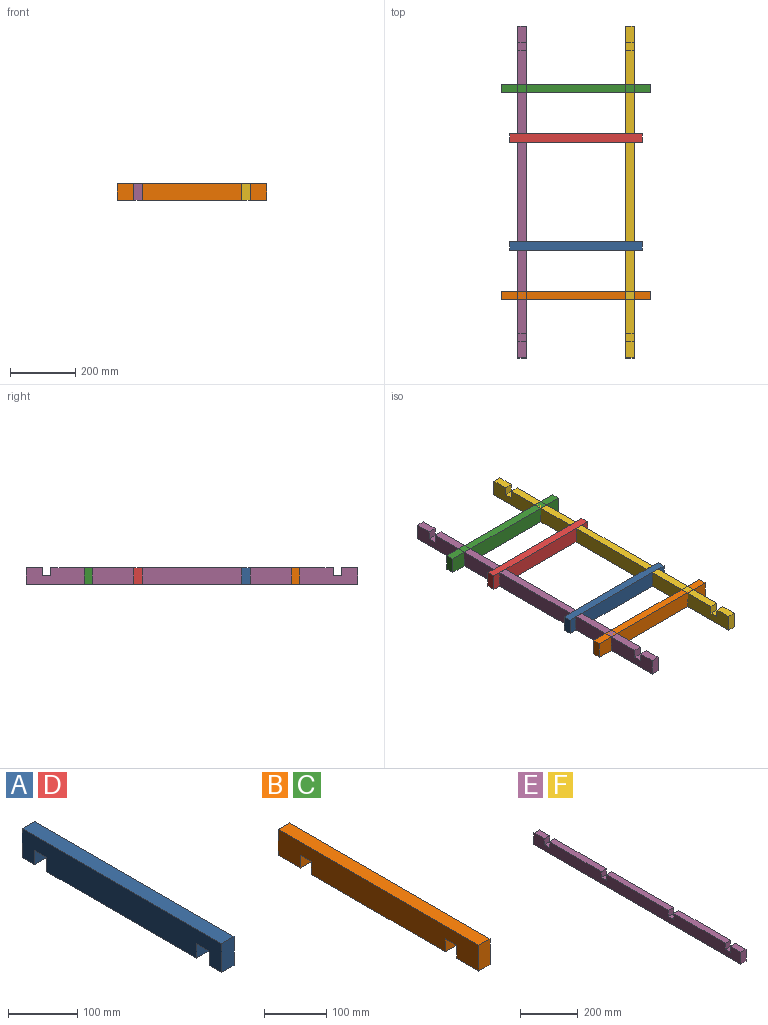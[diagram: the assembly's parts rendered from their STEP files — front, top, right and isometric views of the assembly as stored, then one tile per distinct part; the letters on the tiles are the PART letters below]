
ASSEMBLY  parts=6 mates=2
PART A: 14 faces, bbox 25.4x406.4x50.8 mm
  f0: plane 304.8x25.4mm, normal (0,0,-1), area 7741.9mm2, adj f2,f3,f9,f11
  f1: plane 25.4x25.4mm, normal (0,0,-1), area 645.2mm2, adj f2,f3,f6,f10
  f2: plane 406.4x50.8mm, normal (1,0,0), area 19354.8mm2, adj f0,f1,f4,f5,f6,f7,f8,f9
  f3: plane 406.4x50.8mm, normal (-1,0,0), area 19354.8mm2, adj f0,f1,f4,f5,f6,f7,f8,f9
  f4: plane 50.8x25.4mm, normal (0,-1,0), area 1290.3mm2, adj f2,f3,f5,f7
  f5: plane 25.4x25.4mm, normal (0,0,-1), area 645.2mm2, adj f2,f3,f4,f13
  f6: plane 50.8x25.4mm, normal (0,1,0), area 1290.3mm2, adj f1,f2,f3,f7
  f7: plane 406.4x25.4mm, normal (0,0,1), area 10322.6mm2, adj f2,f3,f4,f6
  f8: plane 25.4x25.4mm, normal (0,0,-1), area 645.2mm2, adj f2,f3,f9,f10
  f9: plane 25.4x25.4mm, normal (0,1,0), area 645.2mm2, adj f0,f2,f3,f8
  f10: plane 25.4x25.4mm, normal (0,-1,0), area 645.2mm2, adj f1,f2,f3,f8
  f11: plane 25.4x25.4mm, normal (0,-1,0), area 645.2mm2, adj f0,f2,f3,f12
  f12: plane 25.4x25.4mm, normal (0,0,-1), area 645.2mm2, adj f2,f3,f11,f13
  f13: plane 25.4x25.4mm, normal (0,1,0), area 645.2mm2, adj f2,f3,f5,f12
PART B: 14 faces, bbox 25.4x457.2x50.8 mm
  f0: plane 304.8x25.4mm, normal (0,0,-1), area 7741.9mm2, adj f2,f3,f9,f11
  f1: plane 50.8x25.4mm, normal (0,0,-1), area 1290.3mm2, adj f2,f3,f6,f10
  f2: plane 457.2x50.8mm, normal (1,0,0), area 21935.4mm2, adj f0,f1,f4,f5,f6,f7,f8,f9
  f3: plane 457.2x50.8mm, normal (-1,0,0), area 21935.4mm2, adj f0,f1,f4,f5,f6,f7,f8,f9
  f4: plane 50.8x25.4mm, normal (0,-1,0), area 1290.3mm2, adj f2,f3,f5,f7
  f5: plane 50.8x25.4mm, normal (0,0,-1), area 1290.3mm2, adj f2,f3,f4,f13
  f6: plane 50.8x25.4mm, normal (0,1,0), area 1290.3mm2, adj f1,f2,f3,f7
  f7: plane 457.2x25.4mm, normal (0,0,1), area 11612.9mm2, adj f2,f3,f4,f6
  f8: plane 25.4x25.4mm, normal (0,0,-1), area 645.2mm2, adj f2,f3,f9,f10
  f9: plane 25.4x25.4mm, normal (0,1,0), area 645.2mm2, adj f0,f2,f3,f8
  f10: plane 25.4x25.4mm, normal (0,-1,0), area 645.2mm2, adj f1,f2,f3,f8
  f11: plane 25.4x25.4mm, normal (0,-1,0), area 645.2mm2, adj f0,f2,f3,f12
  f12: plane 25.4x25.4mm, normal (0,0,-1), area 645.2mm2, adj f2,f3,f11,f13
  f13: plane 25.4x25.4mm, normal (0,1,0), area 645.2mm2, adj f2,f3,f5,f12
PART C: same geometry as B
PART D: same geometry as A
PART E: 22 faces, bbox 25.4x1016x50.8 mm
  f0: plane 50.8x25.4mm, normal (0,0,1), area 1290.3mm2, adj f2,f3,f8,f18
  f1: plane 254x25.4mm, normal (0,0,1), area 6451.6mm2, adj f2,f3,f13,f20
  f2: plane 1016x50.8mm, normal (1,0,0), area 49032.2mm2, adj f0,f1,f4,f5,f6,f7,f8,f9
  f3: plane 1016x50.8mm, normal (-1,0,0), area 49032.2mm2, adj f0,f1,f4,f5,f6,f7,f8,f9
  f4: plane 304.8x25.4mm, normal (0,0,1), area 7741.9mm2, adj f2,f3,f12,f15
  f5: plane 254x25.4mm, normal (0,0,1), area 6451.6mm2, adj f2,f3,f11,f16
  f6: plane 50.8x25.4mm, normal (0,-1,0), area 1290.3mm2, adj f2,f3,f7,f9
  f7: plane 1016x25.4mm, normal (0,0,-1), area 25806.4mm2, adj f2,f3,f6,f8
  f8: plane 50.8x25.4mm, normal (0,1,0), area 1290.3mm2, adj f0,f2,f3,f7
  f9: plane 50.8x25.4mm, normal (0,0,1), area 1290.3mm2, adj f2,f3,f6,f21
  f10: plane 25.4x25.4mm, normal (0,0,1), area 645.2mm2, adj f2,f3,f11,f12
  f11: plane 25.4x25.4mm, normal (0,-1,0), area 645.2mm2, adj f2,f3,f5,f10
  f12: plane 25.4x25.4mm, normal (0,1,0), area 645.2mm2, adj f2,f3,f4,f10
  f13: plane 25.4x25.4mm, normal (0,1,0), area 645.2mm2, adj f1,f2,f3,f14
  f14: plane 25.4x25.4mm, normal (0,0,1), area 645.2mm2, adj f2,f3,f13,f15
  f15: plane 25.4x25.4mm, normal (0,-1,0), area 645.2mm2, adj f2,f3,f4,f14
  f16: plane 25.4x25.4mm, normal (0,1,0), area 645.2mm2, adj f2,f3,f5,f17
  f17: plane 25.4x25.4mm, normal (0,0,1), area 645.2mm2, adj f2,f3,f16,f18
  f18: plane 25.4x25.4mm, normal (0,-1,0), area 645.2mm2, adj f0,f2,f3,f17
  f19: plane 25.4x25.4mm, normal (0,0,1), area 645.2mm2, adj f2,f3,f20,f21
  f20: plane 25.4x25.4mm, normal (0,-1,0), area 645.2mm2, adj f1,f2,f3,f19
  f21: plane 25.4x25.4mm, normal (0,1,0), area 645.2mm2, adj f2,f3,f9,f19
PART F: same geometry as E
PLACE A rot(axis=(0,0,-1),90deg) t=(-33.85,-124.89,-72.4)mm
PLACE B rot(axis=(0,0,1),90deg) t=(-33.85,-302.69,-72.4)mm
PLACE C rot(axis=(0,0,-1),90deg) t=(-33.85,357.71,-72.4)mm
PLACE D rot(axis=(0,0,-1),90deg) t=(-33.85,205.31,-72.4)mm
PLACE E t=(-211.65,27.51,-72.4)mm
PLACE F t=(118.55,27.51,-72.4)mm fixed
MATE fastened A.f12 <-> E.f14  axis (0,0,-1) through (-198.95,-137.59,-72.4)mm
MATE fastened D.f12 <-> E.f10  axis (0,0,-1) through (-198.95,192.61,-72.4)mm
